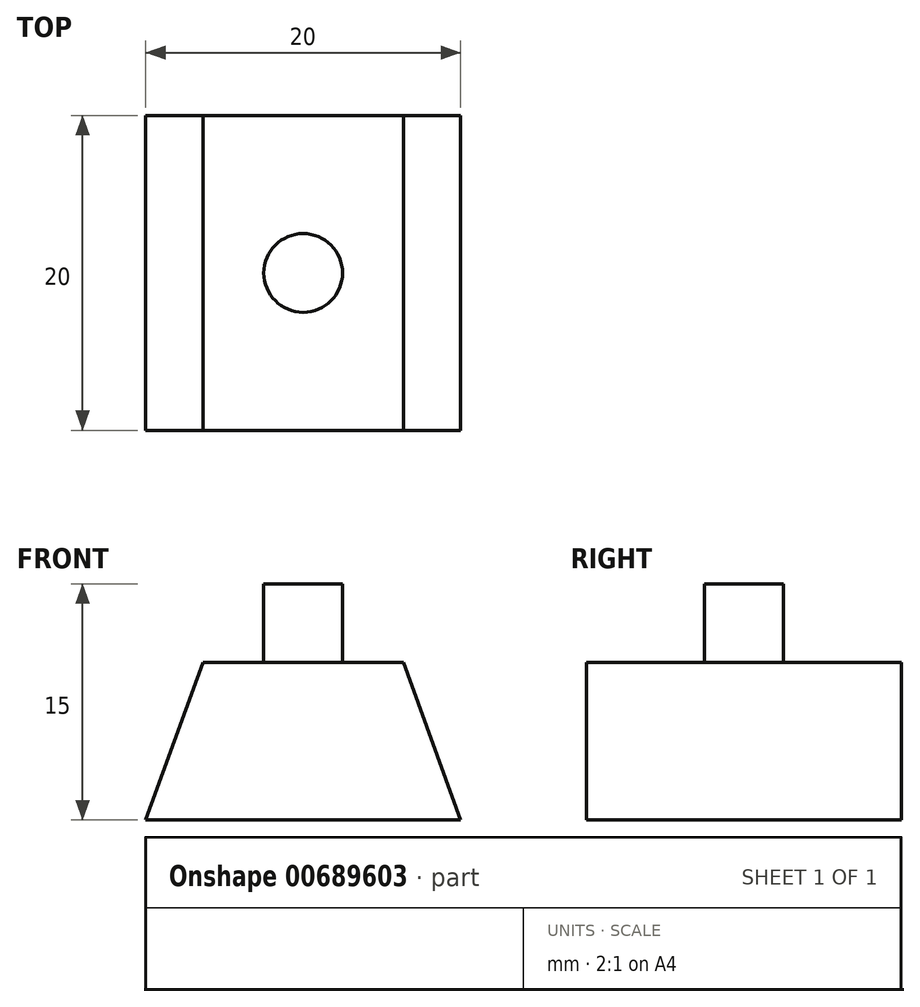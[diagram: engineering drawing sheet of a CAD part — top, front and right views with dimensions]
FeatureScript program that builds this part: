
annotation { "Feature Type Name" : "Feature", "Feature Type Description" : "" }
export const myFeature = defineFeature(function(context is Context, id is Id, definition is map)
    precondition{}
    {
        {
            var Q0;
            Q0=qCreatedBy(makeId("Front.planeOp"),FACE);
            var sketch = newSketch(context, id + "F0", { "sketchPlane" : qUnion([Q0])});
            skLineSegment(sketch, "E0.bottom", {"start": v(0, 0) * mm, "end": v(-20, 0) * mm});
            skLineSegment(sketch, "E0.top", {"start": v(-3.64, 10) * mm, "end": v(-16.36, 10) * mm});
            skPoint(sketch, "E1.middle", {"position": v(-10, 10) * mm});
            skLineSegment(sketch, "E2", {"start": v(-3.64, 10) * mm, "end": v(0, 0) * mm});
            skLineSegment(sketch, "E3", {"start": v(-20, 0) * mm, "end": v(-16.36, 10) * mm});
            skPoint(sketch, "E0.right.end.orphan", {"position": v(-20, 10) * mm});
            skPoint(sketch, "E4.orphan", {"position": v(0, 10) * mm});
            skPoint(sketch, "E5.orphan", {"position": v(-3.64, 9.07) * mm});
            skPoint(sketch, "E1.right.end.orphan", {"position": v(-3.64, 10.93) * mm});
            skPoint(sketch, "E6.orphan", {"position": v(-16.36, 10.93) * mm});
            skPoint(sketch, "E1.left.start.orphan", {"position": v(-16.36, 9.07) * mm});
            skPoint(sketch, "E7.orphan", {"position": v(-7.5, 7.5) * mm});
            skPoint(sketch, "E8.orphan", {"position": v(-12.5, 7.5) * mm});
            skSolve(sketch);
        }
        {
            var Q0;
            Q0=makeQuery(id+"F0.imprint","IMPRINT",FACE,{"disambiguationData":[TD([[makeQuery(id+"F0.imprint","IMPRINT",EDGE,{"derivedFrom":sQuery(id+"F0.wireOp",EDGE,"E0.bottom")}),-1.0]])]});
            var Q1;
            Q1=makeQuery(id+"F0.imprint","IMPRINT",FACE,{"disambiguationData":[TD([[makeQuery(id+"F0.imprint","IMPRINT",EDGE,{"derivedFrom":sQuery(id+"F0.wireOp",EDGE,"0sWYtCi8-Ck9n-oRpk-OtYw-Svaxw7kAYALa.bottom")}),-1.0]])]});
            extrude(context, id + "F1", {"entities" : qUnion([Q0, Q1]), "depth" : 20 * mm, "offsetDistance" : 25 * mm});
        }
        {
            var Q0;
            Q0=makeQuery(id+"F1.opExtrude","SWEPT_FACE",FACE,{"disambiguationData":[OSD([sQuery(id+"F0.wireOp",EDGE,"E0.top")])]});
            var sketch = newSketch(context, id + "F2", { "sketchPlane" : qUnion([Q0])});
            skCircle(sketch, "E9", {"center": v(-10, -10) * mm, "radius": 2.5 * mm});
            skPoint(sketch, "E10.orphan", {"position": v(-16.36, 0) * mm});
            skPoint(sketch, "E11.orphan", {"position": v(-3.64, -20) * mm});
            skSolve(sketch);
        }
        {
            var Q0;
            Q0=makeQuery(id+"F2.imprint","IMPRINT",FACE,{"disambiguationData":[TD([[makeQuery(id+"F2.imprint","IMPRINT",EDGE,{"derivedFrom":sQuery(id+"F2.wireOp",EDGE,"E9")}),1.0]])]});
            extrude(context, id + "F3", {"entities" : qUnion([Q0]), "operationType" : NewBodyOperationType.ADD, "depth" : 5 * mm, "offsetDistance" : 25 * mm});
        }
    });
